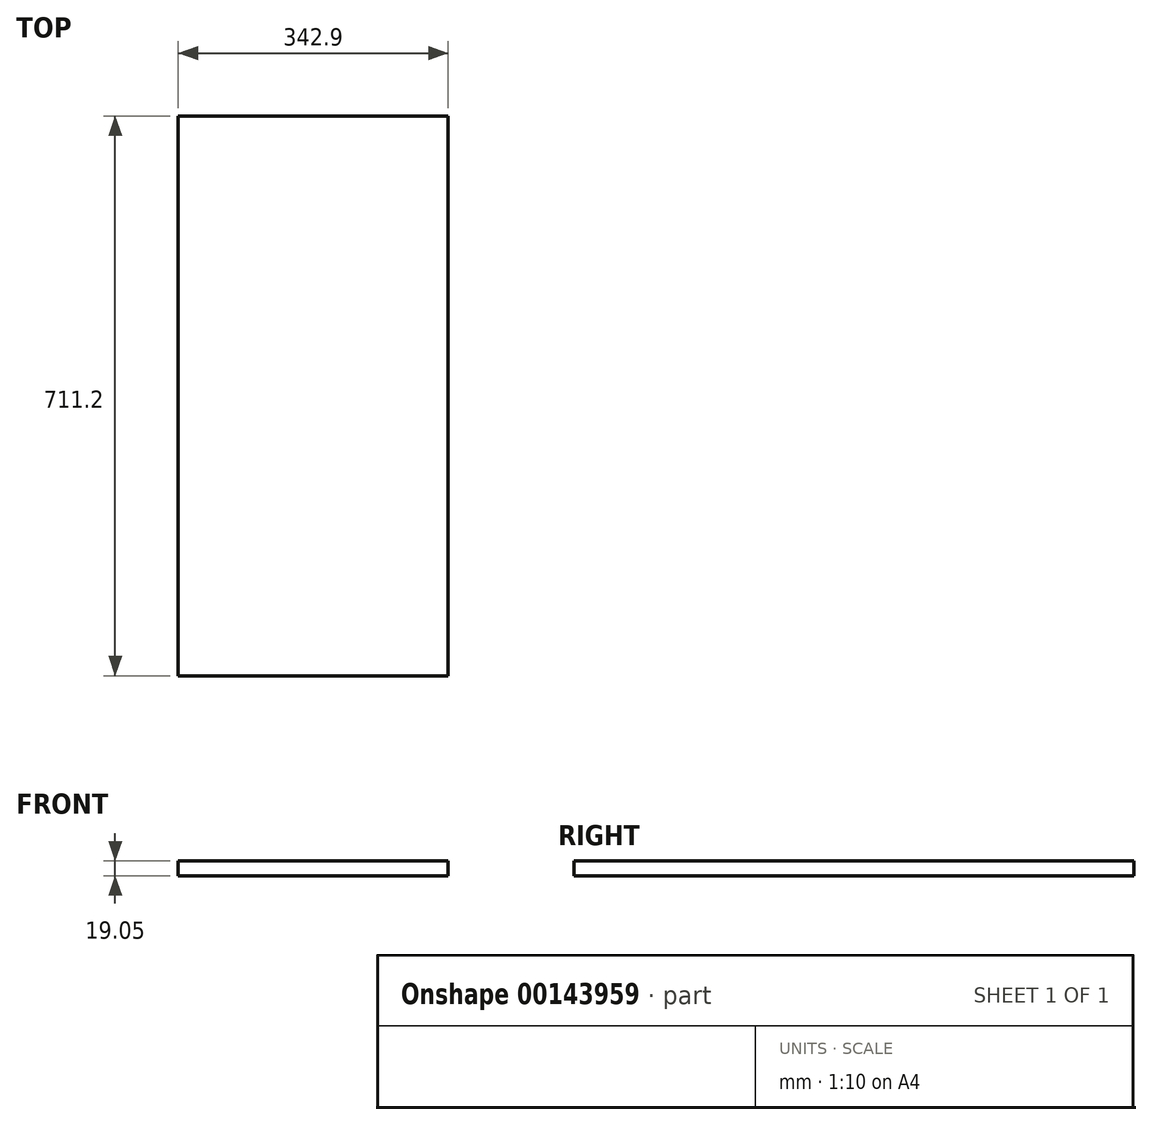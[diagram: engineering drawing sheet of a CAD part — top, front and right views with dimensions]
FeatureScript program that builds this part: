
annotation { "Feature Type Name" : "Feature", "Feature Type Description" : "" }
export const myFeature = defineFeature(function(context is Context, id is Id, definition is map)
    precondition{}
    {
        {
            var Q0;
            Q0=qCreatedBy(makeId("Top.planeOp"),FACE);
            var sketch = newSketch(context, id + "F0", { "sketchPlane" : qUnion([Q0])});
            skLineSegment(sketch, "E0.bottom", {"start": v(151.84, -52.15) * mm, "end": v(-191.06, -52.15) * mm});
            skLineSegment(sketch, "E0.top", {"start": v(151.84, 659.05) * mm, "end": v(-191.06, 659.05) * mm});
            skLineSegment(sketch, "E0.left", {"start": v(151.84, -52.15) * mm, "end": v(151.84, 659.05) * mm});
            skLineSegment(sketch, "E0.right", {"start": v(-191.06, -52.15) * mm, "end": v(-191.06, 659.05) * mm});
            skSolve(sketch);
        }
        {
            var Q0;
            Q0=makeQuery(id+"F0.imprint","IMPRINT",FACE,{"disambiguationData":[TD([[makeQuery(id+"F0.imprint","IMPRINT",EDGE,{"derivedFrom":sQuery(id+"F0.wireOp",EDGE,"E0.bottom")}),-1.0]])]});
            extrude(context, id + "F1", {"entities" : qUnion([Q0]), "depth" : 19.05 * mm});
        }
    });
